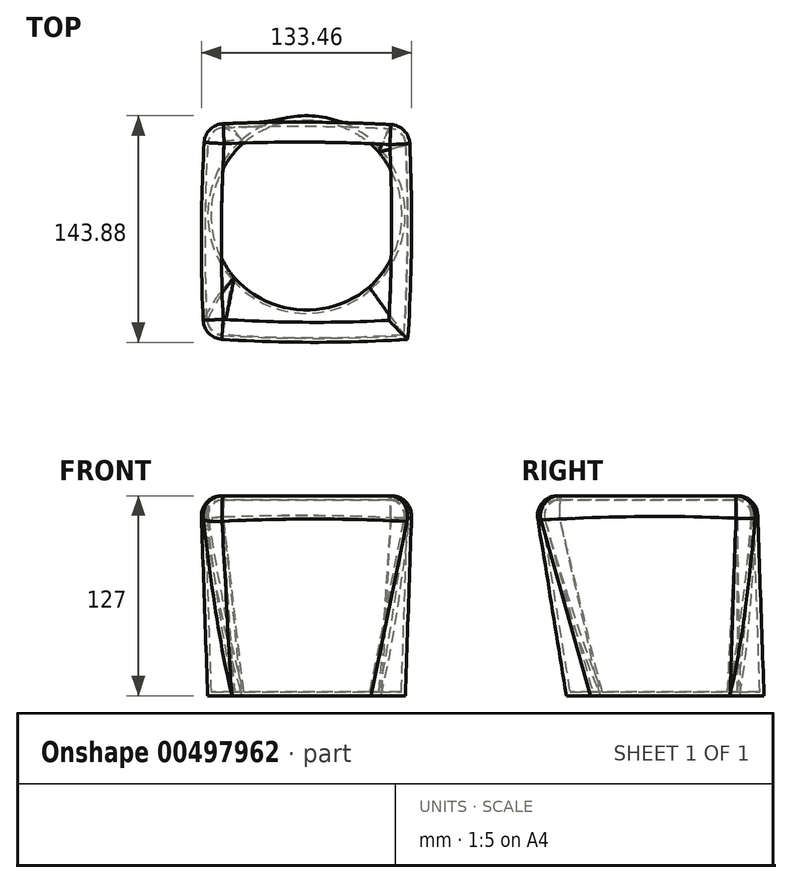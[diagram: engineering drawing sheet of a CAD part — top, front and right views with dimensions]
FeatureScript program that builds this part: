
annotation { "Feature Type Name" : "Feature", "Feature Type Description" : "" }
export const myFeature = defineFeature(function(context is Context, id is Id, definition is map)
    precondition{}
    {
        {
            var Q0;
            Q0=qCreatedBy(makeId("Top.planeOp"),FACE);
            var sketch = newSketch(context, id + "F0", { "sketchPlane" : qUnion([Q0])});
            skCircle(sketch, "E0", {"center": v(0, 0) * mm, "radius": 62.76 * mm});
            skSolve(sketch);
        }
        {
            var Q0;
            Q0=qCreatedBy(makeId("Top.planeOp"),FACE);
            cPlane(context, id + "F1", {"entities" : qUnion([Q0]), "cplaneType" : CPlaneType.OFFSET, "offset" : 127 * mm, "width" : 152.4 * mm, "height" : 152.4 * mm});
        }
        {
            var Q0;
            Q0=qCreatedBy(id+"F1.planeOp",FACE);
            var sketch = newSketch(context, id + "F2", { "sketchPlane" : qUnion([Q0])});
            skLineSegment(sketch, "E1.bottom", {"start": v(67.18, 58.3) * mm, "end": v(-67.18, 58.3) * mm});
            skLineSegment(sketch, "E1.top", {"start": v(67.18, -83.35) * mm, "end": v(-67.18, -83.35) * mm});
            skLineSegment(sketch, "E1.left", {"start": v(67.18, 58.3) * mm, "end": v(67.18, -83.35) * mm});
            skLineSegment(sketch, "E1.right", {"start": v(-67.18, 58.3) * mm, "end": v(-67.18, -83.35) * mm});
            skPoint(sketch, "E1.middle", {"position": v(0, -12.53) * mm});
            skSolve(sketch);
        }
        {
            var Q0;
            Q0=makeQuery(id+"F2.imprint","IMPRINT",FACE,{"disambiguationData":[TD([[makeQuery(id+"F2.imprint","IMPRINT",EDGE,{"derivedFrom":sQuery(id+"F2.wireOp",EDGE,"E1.bottom")}),1.0]])]});
            var Q1;
            Q1=makeQuery(id+"F0.imprint","IMPRINT",FACE,{"disambiguationData":[TD([[makeQuery(id+"F0.imprint","IMPRINT",EDGE,{"derivedFrom":sQuery(id+"F0.wireOp",EDGE,"E0")}),1.0]])]});
            loft(context, id + "F3", {"sheetProfilesArray" : [{ "sheetProfileEntities" : qUnion([Q0]) }, { "sheetProfileEntities" : qUnion([Q1]) }]});
        }
        {
            var Q0;
            Q0=makeQuery(id+"F3.opLoft","SWEPT_EDGE",EDGE,{"disambiguationData":[OSD([sQuery(id+"F0.wireOp",EDGE,"E0"),sQuery(id+"F2.wireOp",EDGE,"E1.top"),sQuery(id+"F2.wireOp",EDGE,"E1.left"),sQuery(id+"F2.wireOp",EDGE,"E1.right")])]});
            var Q1;
            Q1=makeQuery(id+"F3.opLoft","SWEPT_EDGE",EDGE,{"disambiguationData":[OSD([sQuery(id+"F0.wireOp",EDGE,"E0"),sQuery(id+"F2.wireOp",EDGE,"E1.bottom"),sQuery(id+"F2.wireOp",EDGE,"E1.top"),sQuery(id+"F2.wireOp",EDGE,"E1.left")])]});
            var Q2;
            Q2=makeQuery(id+"F3.opLoft","SWEPT_EDGE",EDGE,{"disambiguationData":[OSD([sQuery(id+"F2.wireOp",EDGE,"E1.bottom"),sQuery(id+"F2.wireOp",EDGE,"E1.left")])]});
            var Q3;
            Q3=makeQuery(id+"F3.opLoft","SWEPT_EDGE",EDGE,{"disambiguationData":[OSD([sQuery(id+"F0.wireOp",EDGE,"E0"),sQuery(id+"F2.wireOp",EDGE,"E1.bottom"),sQuery(id+"F2.wireOp",EDGE,"E1.top"),sQuery(id+"F2.wireOp",EDGE,"E1.right")])]});
            var Q4;
            Q4=makeQuery(id+"F3.opLoft","MID_CAP_EDGE",EDGE,{"disambiguationData":[OSD([sQuery(id+"F2.wireOp",EDGE,"E1.bottom"),sQuery(id+"F2.wireOp",EDGE,"E1.top"),sQuery(id+"F2.wireOp",EDGE,"E1.right")])],"capPos":0.0});
            var Q5;
            Q5=makeQuery(id+"F3.opLoft","MID_CAP_EDGE",EDGE,{"disambiguationData":[OSD([sQuery(id+"F2.wireOp",EDGE,"E1.bottom"),sQuery(id+"F2.wireOp",EDGE,"E1.left"),sQuery(id+"F2.wireOp",EDGE,"E1.right")])],"capPos":0.0});
            var Q6;
            Q6=makeQuery(id+"F3.opLoft","MID_CAP_EDGE",EDGE,{"disambiguationData":[OSD([sQuery(id+"F2.wireOp",EDGE,"E1.bottom"),sQuery(id+"F2.wireOp",EDGE,"E1.top"),sQuery(id+"F2.wireOp",EDGE,"E1.left")])],"capPos":0.0});
            var Q7;
            Q7=makeQuery(id+"F3.opLoft","MID_CAP_EDGE",EDGE,{"disambiguationData":[OSD([sQuery(id+"F2.wireOp",EDGE,"E1.top"),sQuery(id+"F2.wireOp",EDGE,"E1.left"),sQuery(id+"F2.wireOp",EDGE,"E1.right")])],"capPos":0.0});
            fillet(context, id + "F4", {"entities" : qUnion([Q0, Q1, Q2, Q3, Q4, Q5, Q6, Q7]), "radius" : 12.7 * mm, "tangentPropagation" : true, "allowEdgeOverflow" : false});
        }
        {
            var Q0;
            Q0=makeQuery(id+"F3.opLoft","CAP_FACE",FACE,{"disambiguationData":[OSD([makeQuery(id+"F2.imprint","IMPRINT",FACE,{"disambiguationData":[TD([[makeQuery(id+"F2.imprint","IMPRINT",EDGE,{"derivedFrom":sQuery(id+"F2.wireOp",EDGE,"E1.bottom")}),1.0]])]})])],"isStart":true});
            shell(context, id + "F5", {"entities" : qUnion([Q0]), "thickness" : 2.54 * mm});
        }
    });
